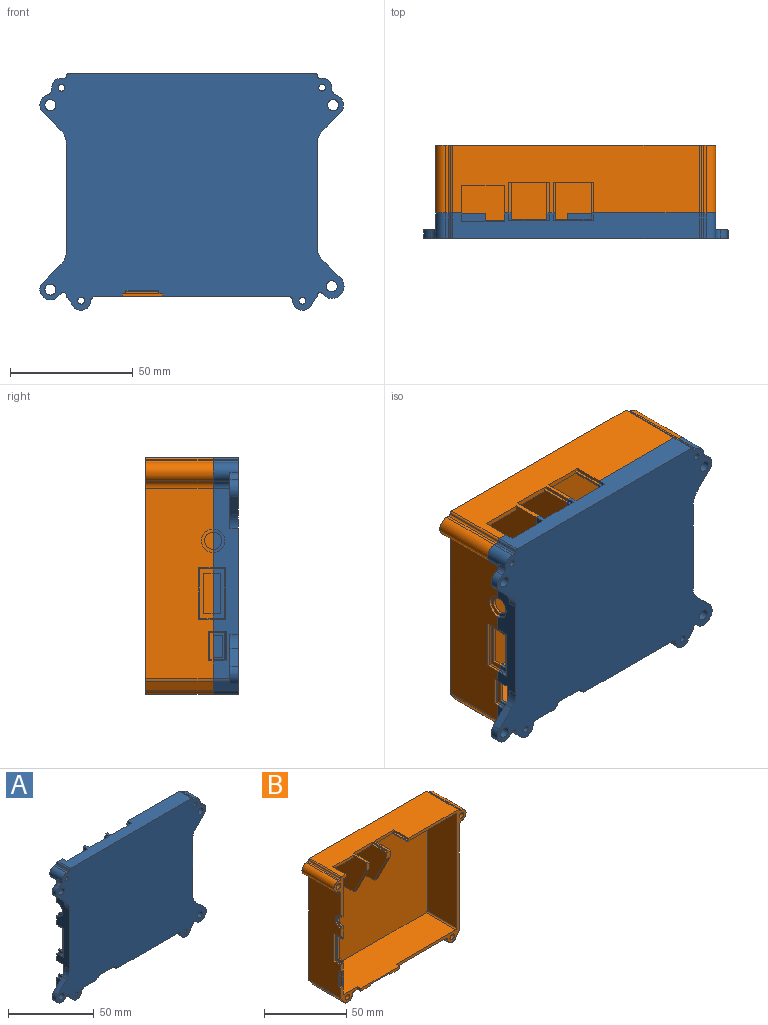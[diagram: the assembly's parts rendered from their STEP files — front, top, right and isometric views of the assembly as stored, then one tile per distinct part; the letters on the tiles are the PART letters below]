
ASSEMBLY  parts=2 mates=1
PART A: 157 faces, bbox 123.7x10.3x96.3 mm
  f0: plane 78.09x10.3mm, normal (1,0,0), area 678.6mm2, adj f1,f3,f124,f130,f138,f141,f144,f147
  f1: cylinder r=3mm len=6.8mm, axis (0,1,0), area 29.1mm2, adj f0,f2,f130,f147
  f2: cylinder r=3.9mm len=10.3mm, axis (0,1,0), area 101.4mm2, adj f1,f3,f123,f130,f136,f147
  f3: plane 123.68x96.25mm, normal (0,-1,0), area 9747mm2, adj f0,f2,f6,f9,f10,f11,f18,f19
  f4: plane 98x86.6mm, normal (0,1,0), area 8334.6mm2, adj f5,f21,f36,f37,f44,f46,f48,f49
  f5: plane 61.85x8.3mm, normal (0,0,1), area 483.4mm2, adj f4,f35,f50,f130,f132,f133
  f6: plane 50.96x10.3mm, normal (0,0,-1), area 499.3mm2, adj f3,f32,f50,f126,f130,f132
  f7: plane 22.79x10.75mm, normal (0,1,0), area 100.2mm2, adj f10,f11,f56,f86,f87,f88,f89,f90
  f8: plane 20.07x10.76mm, normal (0,1,0), area 93.7mm2, adj f9,f56,f91,f92,f93,f94,f95,f96
  f9: cylinder r=2.25mm len=4.5mm, axis (0,-1,0), area 49.5mm2, adj f3,f8
  f10: cylinder r=2.25mm len=4.5mm, axis (0,-1,0), area 49.5mm2, adj f3,f7
  f11: cylinder r=3.9mm len=10.3mm, axis (0,-1,0), area 101.4mm2, adj f3,f7,f14,f86,f90,f102
  f12: plane 3x2.8mm, normal (0,1,0), area 7.2mm2, adj f20,f23,f25,f30,f112,f113
  f13: plane 3.5x3mm, normal (0,1,0), area 8.1mm2, adj f24,f27,f29,f30,f113,f114,f117,f119
  f14: plane 30.25x10.45mm, normal (0,1,0), area 99.5mm2, adj f11,f19,f21,f30,f52,f53,f54,f55
  f15: plane 8.65x2.5mm, normal (0,1,0), area 15.1mm2, adj f52,f56,f58,f59,f60,f61,f63,f64
  f16: plane 9.75x2.5mm, normal (0,1,0), area 16.8mm2, adj f52,f53,f54,f55,f56,f61,f64,f70
  f17: plane 15.1x14.15mm, normal (0,1,0), area 78mm2, adj f18,f31,f49,f51,f52,f56,f60,f62
  f18: cylinder r=1.4mm len=10.3mm, axis (0,-1,0), area 90.6mm2, adj f3,f17
  f19: cylinder r=1.4mm len=10.3mm, axis (0,-1,0), area 90.6mm2, adj f3,f14
  f20: plane 3.6x3mm, normal (-1,0,0), area 8.7mm2, adj f12,f21,f22,f25,f30,f111
  f21: plane 97x8.3mm, normal (0,0,-1), area 654.8mm2, adj f4,f14,f20,f22,f23,f26,f27,f28
  f22: plane 2.8x2mm, normal (0,-0.45,-0.89), area 6.3mm2, adj f20,f21,f23,f25
  f23: plane 2.55x1.8mm, normal (1,0,0), area 3.5mm2, adj f12,f21,f22,f25,f113,f118
  f24: plane 3.5x0.55mm, normal (0,0,-1), area 1.9mm2, adj f13,f26,f27,f119
  f25: plane 2.8x0.55mm, normal (0,0,-1), area 1.5mm2, adj f12,f20,f22,f23
  f26: plane 3.5x2mm, normal (0,-0.45,-0.89), area 7.8mm2, adj f21,f24,f27,f119
  f27: plane 2.55x1.8mm, normal (1,0,0), area 3.5mm2, adj f13,f21,f24,f26,f28,f29
  f28: plane 14.5x0.8mm, normal (0,1,0), area 11.6mm2, adj f21,f27,f29,f131
  f29: plane 16.5x3.17mm, normal (0,0,1), area 16.5mm2, adj f13,f27,f28,f116,f117,f129,f130,f131
  f30: plane 100.4x10.3mm, normal (0,0,1), area 866.9mm2, adj f3,f12,f13,f14,f20,f100,f110,f111
  f31: plane 10.76x10.3mm, normal (0,0,-1), area 85.3mm2, adj f3,f17,f99,f104,f105,f109
  f32: plane 7.3x1mm, normal (-1,0,0), area 7.3mm2, adj f3,f6,f33,f50
  f33: plane 7.3x1.5mm, normal (0,0,-1), area 10.9mm2, adj f3,f32,f35,f50
  f34: plane 7.3x1.5mm, normal (0,0,-1), area 11mm2, adj f3,f105,f106,f109
  f35: plane 7.3x1mm, normal (-1,0,0), area 7.3mm2, adj f3,f5,f33,f36,f50
  f36: cylinder r=0.5mm len=2mm, axis (0,-1,0), area 1.6mm2, adj f3,f4,f35,f108
  f37: cone r=3.15mm half-angle=45deg, axis (0,-1,0), area 14mm2, adj f4,f38
  f38: cylinder r=2.9mm len=5.8mm, axis (0,1,0), area 63.8mm2, adj f37,f40
  f39: plane 5.8x5.8mm, normal (0,1,0), area 23.3mm2, adj f43,f151
  f40: plane 5.8x5.8mm, normal (0,1,0), area 23.3mm2, adj f38,f153
  f41: plane 5.8x5.8mm, normal (0,1,0), area 23.3mm2, adj f45,f149
  f42: plane 5.8x5.8mm, normal (0,1,0), area 23.3mm2, adj f47,f155
  f43: cylinder r=2.9mm len=5.8mm, axis (0,1,0), area 63.8mm2, adj f39,f44
  f44: cone r=3.15mm half-angle=45deg, axis (0,-1,0), area 14mm2, adj f4,f43
  f45: cylinder r=2.9mm len=5.8mm, axis (0,1,0), area 63.8mm2, adj f41,f46
  f46: cone r=3.15mm half-angle=45deg, axis (0,-1,0), area 14mm2, adj f4,f45
  f47: cylinder r=2.9mm len=5.8mm, axis (0,1,0), area 63.8mm2, adj f42,f48
  f48: cone r=3.15mm half-angle=45deg, axis (0,-1,0), area 14mm2, adj f4,f47
  f49: plane 21.65x8.3mm, normal (0,0,1), area 149.7mm2, adj f4,f17,f51,f104,f105,f106
  f50: plane 10x2mm, normal (0,1,0), area 18.5mm2, adj f5,f6,f32,f33,f35,f132
  f51: cylinder r=0.5mm len=8.3mm, axis (0,1,0), area 6.5mm2, adj f4,f17,f49,f52
  f52: plane 85.6x8.3mm, normal (1,0,0), area 494.1mm2, adj f4,f14,f15,f16,f17,f51,f53,f65
  f53: cylinder r=3.5mm len=7mm, axis (-1,0,0), area 11mm2, adj f14,f16,f52,f54
  f54: plane 9.5x4.75mm, normal (-1,0,0), area 16.2mm2, adj f14,f16,f53,f55
  f55: cylinder r=4.75mm len=9.5mm, axis (-1,0,0), area 14.9mm2, adj f14,f16,f54,f56
  f56: plane 77.46x10.3mm, normal (-1,0,0), area 472.5mm2, adj f3,f7,f8,f14,f15,f16,f17,f55
  f57: plane 10.3x0.18mm, normal (-1,0,0), area 1.9mm2, adj f3,f14,f100,f101
  f58: plane 5.12x1mm, normal (0,0,1), area 5.1mm2, adj f15,f56,f59,f84
  f59: plane 5.12x0.5mm, normal (-0.71,0,0.71), area 3.4mm2, adj f15,f58,f61,f85
  f60: plane 11x4.75mm, normal (-1,0,0), area 18.5mm2, adj f15,f17,f62,f68,f69,f76,f79,f80
  f61: plane 20x4.62mm, normal (-1,0,0), area 40.9mm2, adj f15,f16,f59,f70,f71,f72,f82,f85
  f62: plane 3.75x1mm, normal (0,0,1), area 3.8mm2, adj f17,f60,f63,f69
  f63: plane 14x5.25mm, normal (1,0,0), area 39.8mm2, adj f15,f17,f62,f65,f66,f67,f68,f69
  f64: plane 23x3.62mm, normal (1,0,0), area 31.8mm2, adj f15,f16,f70,f71,f72,f73,f74,f75
  f65: plane 5.75x0.5mm, normal (0.71,0,-0.71), area 3.9mm2, adj f17,f52,f63,f66
  f66: plane 15x0.5mm, normal (0.71,-0.71,0), area 10.3mm2, adj f52,f63,f65,f67
  f67: plane 5.75x0.5mm, normal (0.71,0,0.71), area 3.9mm2, adj f15,f52,f63,f66
  f68: plane 3.75x1mm, normal (0,0,-1), area 3.8mm2, adj f15,f60,f63,f69
  f69: plane 9x1mm, normal (0,1,0), area 9mm2, adj f60,f62,f63,f68
  f70: plane 3.12x1mm, normal (0,0,-1), area 3.1mm2, adj f16,f61,f64,f71
  f71: plane 16.5x1mm, normal (0,1,0), area 16.5mm2, adj f61,f64,f70,f72
  f72: plane 3.12x1mm, normal (0,0,1), area 3.1mm2, adj f15,f61,f64,f71
  f73: plane 4.62x0.5mm, normal (0.71,0,-0.71), area 2.9mm2, adj f15,f52,f64,f74
  f74: plane 24x1mm, normal (0.89,-0.45,0), area 26.3mm2, adj f52,f64,f73,f75
  f75: plane 4.62x0.5mm, normal (0.71,0,0.71), area 2.9mm2, adj f16,f52,f64,f74
  f76: plane 5.25x0.5mm, normal (-0.71,0,-0.71), area 3.5mm2, adj f15,f60,f77,f79
  f77: plane 5.25x1mm, normal (0,0,-1), area 5.2mm2, adj f15,f56,f76,f78
  f78: plane 12x1mm, normal (0,1,0), area 12mm2, adj f56,f77,f79,f81
  f79: plane 12x0.5mm, normal (-0.71,0.71,0), area 8.1mm2, adj f60,f76,f78,f80
  f80: plane 5.25x0.5mm, normal (-0.71,0,0.71), area 3.5mm2, adj f17,f60,f79,f81
  f81: plane 5.25x1mm, normal (0,0,1), area 5.2mm2, adj f17,f56,f78,f80
  f82: plane 5.12x0.5mm, normal (-0.71,0,-0.71), area 3.4mm2, adj f16,f61,f83,f85
  f83: plane 5.12x1mm, normal (0,0,-1), area 5.1mm2, adj f16,f56,f82,f84
  f84: plane 21x1mm, normal (0,1,0), area 21mm2, adj f56,f58,f83,f85
  f85: plane 21x0.5mm, normal (-0.71,0.71,0), area 14.5mm2, adj f59,f61,f82,f84
  f86: cylinder r=3mm len=6.8mm, axis (0,-1,0), area 29.1mm2, adj f7,f11,f14,f56
  f87: cylinder r=8mm len=5.66mm, axis (0,-1,0), area 22mm2, adj f3,f7,f56,f88
  f88: plane 7.16x7.16mm, normal (-0.71,0,-0.71), area 35.5mm2, adj f3,f7,f87,f89
  f89: cylinder r=4.25mm len=7.02mm, axis (0,-1,0), area 30mm2, adj f3,f7,f88,f90
  f90: cylinder r=3mm len=3.5mm, axis (0,-1,0), area 13.4mm2, adj f3,f7,f11,f89
  f91: cylinder r=8mm len=5.66mm, axis (0,1,0), area 22mm2, adj f3,f8,f56,f92
  f92: plane 7.16x7.16mm, normal (-0.71,0,0.71), area 35.5mm2, adj f3,f8,f91,f93
  f93: cylinder r=4.25mm len=7.26mm, axis (0,-1,0), area 46.7mm2, adj f3,f8,f92,f94
  f94: plane 3.5x1.45mm, normal (0.71,0,-0.71), area 7.2mm2, adj f3,f8,f93,f95
  f95: cylinder r=1.2mm len=3.5mm, axis (0,-1,0), area 9.6mm2, adj f3,f8,f94,f96
  f96: cylinder r=2mm len=10.3mm, axis (0,-1,0), area 12.1mm2, adj f3,f8,f17,f56,f95,f97
  f97: plane 10.3x3.48mm, normal (-0.82,0,-0.58), area 43.8mm2, adj f3,f17,f96,f98
  f98: cylinder r=3.9mm len=10.3mm, axis (0,-1,0), area 99.9mm2, adj f3,f17,f97,f99
  f99: cylinder r=2mm len=10.3mm, axis (0,-1,0), area 31.5mm2, adj f3,f17,f31,f98
  f100: cylinder r=0.8mm len=10.3mm, axis (0,1,0), area 12.9mm2, adj f3,f14,f30,f57
  f101: cylinder r=0.8mm len=10.3mm, axis (0,1,0), area 12.9mm2, adj f3,f14,f57,f102
  f102: plane 10.3x1.2mm, normal (0,0,1), area 12.4mm2, adj f3,f11,f14,f101
  f103: cylinder r=0.5mm len=8.3mm, axis (0,-1,0), area 6.5mm2, adj f4,f14,f21,f52
  f104: plane 3x2mm, normal (1,0,0), area 6mm2, adj f17,f31,f49,f105
  f105: plane 10x2mm, normal (0,1,0), area 18.5mm2, adj f31,f34,f49,f104,f106,f109
  f106: plane 7.3x1mm, normal (1,0,0), area 7.3mm2, adj f3,f34,f49,f105,f107
  f107: cylinder r=0.5mm len=2mm, axis (0,-1,0), area 1.6mm2, adj f3,f4,f106,f108
  f108: plane 12.5x2mm, normal (0,0,-1), area 25mm2, adj f3,f4,f36,f107
  f109: plane 7.3x1mm, normal (1,0,0), area 7.3mm2, adj f3,f31,f34,f105
  f110: plane 3.6x2mm, normal (1,0,0), area 7.2mm2, adj f14,f21,f30,f111
  f111: plane 17.4x2mm, normal (0,1,0), area 34.8mm2, adj f20,f21,f30,f110
  f112: plane 3.17x1.2mm, normal (1,0,0), area 3.8mm2, adj f12,f30,f113,f115
  f113: plane 16.5x3.17mm, normal (0,0,1), area 16.5mm2, adj f12,f13,f23,f112,f114,f115,f118,f119
  f114: plane 3.17x1.2mm, normal (-1,0,0), area 3.8mm2, adj f13,f30,f113,f115
  f115: plane 16.5x1.2mm, normal (0,1,0), area 19.8mm2, adj f30,f112,f113,f114
  f116: plane 16.5x1.2mm, normal (0,1,0), area 19.8mm2, adj f29,f30,f117,f129
  f117: plane 3.17x1.2mm, normal (1,0,0), area 3.8mm2, adj f13,f29,f30,f116
  f118: plane 14.5x0.8mm, normal (0,1,0), area 11.6mm2, adj f21,f23,f113,f119
  f119: plane 2.55x1.8mm, normal (-1,0,0), area 3.5mm2, adj f13,f21,f24,f26,f113,f118
  f120: cylinder r=0.8mm len=10.3mm, axis (0,1,0), area 12.9mm2, adj f3,f30,f121,f130
  f121: plane 10.3x0.18mm, normal (1,0,0), area 1.9mm2, adj f3,f120,f122,f130
  f122: cylinder r=0.8mm len=10.3mm, axis (0,1,0), area 12.9mm2, adj f3,f121,f123,f130
  f123: plane 10.3x1.2mm, normal (0,0,1), area 12.4mm2, adj f2,f3,f122,f130
  f124: plane 10.3x3.99mm, normal (0.82,0,-0.58), area 50.3mm2, adj f0,f3,f125,f130
  f125: cylinder r=3.9mm len=10.3mm, axis (0,1,0), area 99.9mm2, adj f3,f124,f126,f130
  f126: cylinder r=2mm len=10.3mm, axis (0,1,0), area 31.5mm2, adj f3,f6,f125,f130
  f127: cylinder r=1.4mm len=10.3mm, axis (0,1,0), area 90.6mm2, adj f3,f130
  f128: cylinder r=1.4mm len=10.3mm, axis (0,1,0), area 90.6mm2, adj f3,f130
  f129: plane 3.17x1.2mm, normal (-1,0,0), area 3.8mm2, adj f29,f30,f116,f130
  f130: plane 96.25x60.25mm, normal (0,1,0), area 440.9mm2, adj f0,f1,f2,f5,f6,f21,f29,f30
  f131: plane 2.47x0.8mm, normal (-1,0,0), area 2mm2, adj f21,f28,f29,f130
  f132: plane 3x2mm, normal (-1,0,0), area 6mm2, adj f5,f6,f50,f130
  f133: cylinder r=0.5mm len=8.3mm, axis (0,-1,0), area 6.5mm2, adj f4,f5,f130,f134
  f134: plane 85.6x8.3mm, normal (-1,0,0), area 710.5mm2, adj f4,f130,f133,f135
  f135: cylinder r=0.5mm len=8.3mm, axis (0,-1,0), area 6.5mm2, adj f4,f21,f130,f134
  f136: cylinder r=3mm len=3.5mm, axis (0,1,0), area 13.4mm2, adj f2,f3,f139,f147
  f137: cylinder r=2.25mm len=4.5mm, axis (0,1,0), area 49.5mm2, adj f3,f147
  f138: cylinder r=8mm len=5.66mm, axis (0,1,0), area 22mm2, adj f0,f3,f140,f147
  f139: cylinder r=4.25mm len=7.02mm, axis (0,1,0), area 30mm2, adj f3,f136,f140,f147
  f140: plane 7.16x7.16mm, normal (0.71,0,-0.71), area 35.5mm2, adj f3,f138,f139,f147
  f141: cylinder r=8mm len=5.66mm, axis (0,1,0), area 22mm2, adj f0,f3,f142,f148
  f142: plane 6.05x6.05mm, normal (0.71,0,0.71), area 29.9mm2, adj f3,f141,f145,f148
  f143: cylinder r=2.25mm len=4.5mm, axis (0,1,0), area 49.5mm2, adj f3,f148
  f144: cylinder r=1.2mm len=3.5mm, axis (0,1,0), area 9.9mm2, adj f0,f3,f146,f148
  f145: cylinder r=4.99mm len=9.34mm, axis (0,1,0), area 54.9mm2, adj f3,f142,f146,f148
  f146: plane 3.5x1.45mm, normal (-0.71,0,-0.71), area 7.2mm2, adj f3,f144,f145,f148
  f147: plane 22.79x10.75mm, normal (0,1,0), area 100.2mm2, adj f0,f1,f2,f136,f137,f138,f139,f140
  f148: plane 21.05x10.93mm, normal (0,1,0), area 107.2mm2, adj f0,f141,f142,f143,f144,f145,f146
  f149: cylinder r=1mm len=5mm, axis (0,1,0), area 31.4mm2, adj f41,f150
  f150: plane 2x2mm, normal (0,1,0), area 3.1mm2, adj f149
  f151: cylinder r=1mm len=5mm, axis (0,1,0), area 31.4mm2, adj f39,f152
  f152: plane 2x2mm, normal (0,1,0), area 3.1mm2, adj f151
  f153: cylinder r=1mm len=5mm, axis (0,1,0), area 31.4mm2, adj f40,f154
  f154: plane 2x2mm, normal (0,1,0), area 3.1mm2, adj f153
  f155: cylinder r=1mm len=5mm, axis (0,1,0), area 31.4mm2, adj f42,f156
  f156: plane 2x2mm, normal (0,1,0), area 3.1mm2, adj f155
PART B: 110 faces, bbox 113.8x30.5x96.3 mm
  f0: cylinder r=1.9mm len=26mm, axis (0,1,0), area 310.4mm2, adj f84,f107
  f1: cylinder r=1.9mm len=26mm, axis (0,1,0), area 310.4mm2, adj f84,f105
  f2: plane 14.5x13mm, normal (0,0,-1), area 188.5mm2, adj f4,f7,f103,f109
  f3: plane 56.25x25.5mm, normal (0,0,-1), area 1253.1mm2, adj f5,f24,f84,f85,f103,f108
  f4: plane 25.8x25.5mm, normal (-1,0,0), area 537.2mm2, adj f2,f6,f12,f13,f19,f103,f109
  f5: plane 25.8x25.5mm, normal (1,0,0), area 537.2mm2, adj f3,f6,f12,f13,f18,f103,f108
  f6: plane 15x3.5mm, normal (0,0,-1), area 52.5mm2, adj f4,f5,f13,f103
  f7: plane 25.8x25.5mm, normal (1,0,0), area 537.2mm2, adj f2,f11,f22,f29,f40,f103,f109
  f8: cylinder r=1mm len=25.5mm, axis (0,-1,0), area 40.1mm2, adj f25,f27,f30,f103
  f9: cylinder r=1mm len=25.5mm, axis (0,1,0), area 40.1mm2, adj f28,f30,f31,f103
  f10: plane 27x25.5mm, normal (-1,0,0), area 549.8mm2, adj f11,f15,f20,f25,f29,f40,f103
  f11: plane 15x2.8mm, normal (0,0,-1), area 42mm2, adj f7,f10,f40,f103
  f12: plane 6x3.5mm, normal (0,-1,0), area 18.6mm2, adj f4,f5,f13,f15,f16,f17,f18,f19
  f13: plane 21x10.5mm, normal (0,-0.89,-0.45), area 82.2mm2, adj f4,f5,f6,f12
  f14: plane 113.8x96.25mm, normal (0,1,0), area 9301.3mm2, adj f15,f33,f43,f44,f45,f46,f47,f48
  f15: plane 100.4x27.5mm, normal (0,0,1), area 2151.9mm2, adj f10,f12,f14,f16,f17,f20,f21,f23
  f16: plane 12.5x1.2mm, normal (-1,0,0), area 15mm2, adj f12,f15,f19,f109
  f17: plane 12.5x1.2mm, normal (1,0,0), area 15mm2, adj f12,f15,f18,f108
  f18: plane 12.5x1mm, normal (0,0,1), area 12.5mm2, adj f5,f12,f17,f108
  f19: plane 12.5x1mm, normal (0,0,1), area 12.5mm2, adj f4,f12,f16,f109
  f20: plane 17.4x2mm, normal (0,-1,0), area 34.8mm2, adj f10,f15,f21,f25
  f21: plane 11.3x2mm, normal (1,0,0), area 22.6mm2, adj f15,f20,f25,f27
  f22: plane 12.5x1mm, normal (0,0,1), area 12.5mm2, adj f7,f23,f29,f109
  f23: plane 12.5x1.2mm, normal (1,0,0), area 15mm2, adj f15,f22,f29,f109
  f24: plane 12.5x0.8mm, normal (-1,0,0), area 10mm2, adj f3,f41,f84,f108
  f25: plane 25.5x18.95mm, normal (0,0,-1), area 286.6mm2, adj f8,f10,f20,f21,f27,f103
  f26: plane 9.75x2.5mm, normal (0,-1,0), area 16.8mm2, adj f30,f44,f50,f51,f52,f53,f54,f55
  f27: plane 30.25x10.45mm, normal (0,-1,0), area 94.5mm2, adj f8,f15,f21,f25,f30,f43,f44,f45
  f28: plane 32.75x14.2mm, normal (0,-1,0), area 96.1mm2, adj f9,f30,f31,f33,f39,f44,f55,f56
  f29: plane 6x2.8mm, normal (0,-1,0), area 15.6mm2, adj f7,f10,f15,f22,f23,f40
  f30: plane 84.6x25.5mm, normal (1,0,0), area 1951.2mm2, adj f8,f9,f26,f27,f28,f52,f62,f63
  f31: plane 96x28.5mm, normal (0,0,1), area 2548.2mm2, adj f9,f28,f32,f35,f39,f84,f87,f103
  f32: plane 3x2mm, normal (1,0,0), area 6mm2, adj f31,f33,f35,f84
  f33: plane 78.21x30.5mm, normal (0,0,-1), area 2226.2mm2, adj f14,f28,f32,f34,f35,f37,f38,f39
  f34: plane 1.5x1mm, normal (1,0,0), area 1.5mm2, adj f33,f35,f36,f38
  f35: plane 33.4x2mm, normal (0,-1,0), area 50.3mm2, adj f31,f32,f33,f34,f36,f37,f39
  f36: plane 16.5x1.5mm, normal (0,0,-1), area 24.7mm2, adj f34,f35,f37,f38
  f37: plane 1.5x1mm, normal (-1,0,0), area 1.5mm2, adj f33,f35,f36,f38
  f38: plane 16.5x1mm, normal (0,-1,0), area 16.5mm2, adj f33,f34,f36,f37
  f39: plane 3x2mm, normal (-1,0,0), area 6mm2, adj f28,f31,f33,f35
  f40: plane 21x10.5mm, normal (0,-0.89,-0.45), area 65.7mm2, adj f7,f10,f11,f29
  f41: plane 12.5x1mm, normal (0,0,1), area 12.5mm2, adj f24,f42,f84,f108
  f42: plane 12.5x1.2mm, normal (-1,0,0), area 15mm2, adj f15,f41,f84,f108
  f43: cylinder r=0.8mm len=27.5mm, axis (0,1,0), area 34.6mm2, adj f14,f15,f27,f45
  f44: plane 77.46x27.5mm, normal (-1,0,0), area 1946.2mm2, adj f14,f26,f27,f28,f46,f50,f53,f57
  f45: plane 27.5x0.18mm, normal (-1,0,0), area 4.9mm2, adj f14,f27,f43,f49
  f46: cylinder r=3mm len=27.5mm, axis (0,-1,0), area 117.6mm2, adj f14,f27,f44,f47
  f47: cylinder r=3.9mm len=27.5mm, axis (0,1,0), area 321.3mm2, adj f14,f27,f46,f48
  f48: plane 27.5x1.2mm, normal (0,0,1), area 33mm2, adj f14,f27,f47,f49
  f49: cylinder r=0.8mm len=27.5mm, axis (0,1,0), area 34.6mm2, adj f14,f27,f45,f48
  f50: cylinder r=4.75mm len=9.5mm, axis (-1,0,0), area 14.9mm2, adj f26,f27,f44,f51
  f51: plane 9.5x4.75mm, normal (-1,0,0), area 16.2mm2, adj f26,f27,f50,f52
  f52: cylinder r=3.5mm len=7mm, axis (-1,0,0), area 11mm2, adj f26,f27,f30,f51
  f53: plane 5.93x1mm, normal (0,0,-1), area 5.9mm2, adj f26,f44,f54,f58
  f54: plane 5.93x0.5mm, normal (-0.71,0,-0.71), area 4mm2, adj f26,f53,f55,f59
  f55: plane 20x5.43mm, normal (-1,0,0), area 43.8mm2, adj f26,f28,f54,f56,f59,f60,f65,f66
  f56: plane 5.93x0.5mm, normal (-0.71,0,0.71), area 4mm2, adj f28,f55,f57,f59
  f57: plane 5.93x1mm, normal (0,0,1), area 5.9mm2, adj f28,f44,f56,f58
  f58: plane 21x1mm, normal (0,-1,0), area 21mm2, adj f44,f53,f57,f59
  f59: plane 21x0.5mm, normal (-0.71,-0.71,0), area 14.5mm2, adj f54,f55,f56,f58
  f60: plane 3.93x1mm, normal (0,0,-1), area 3.9mm2, adj f26,f55,f61,f66
  f61: plane 23x5.93mm, normal (1,0,0), area 71.5mm2, adj f26,f28,f60,f62,f63,f64,f65,f66
  f62: plane 6.43x0.5mm, normal (0.71,0,0.71), area 4.4mm2, adj f26,f30,f61,f63
  f63: plane 24x0.5mm, normal (0.71,0.71,0), area 16.6mm2, adj f30,f61,f62,f64
  f64: plane 6.43x0.5mm, normal (0.71,0,-0.71), area 4.4mm2, adj f28,f30,f61,f63
  f65: plane 3.93x1mm, normal (0,0,1), area 3.9mm2, adj f28,f55,f61,f66
  f66: plane 16.5x1mm, normal (0,-1,0), area 16.5mm2, adj f55,f60,f61,f65
  f67: plane 2x1mm, normal (0,0,-1), area 2mm2, adj f28,f44,f68,f72
  f68: plane 2x0.5mm, normal (-0.71,0,-0.71), area 1.2mm2, adj f28,f67,f69,f73
  f69: plane 11x1.5mm, normal (-1,0,0), area 16.5mm2, adj f28,f68,f70,f73
  f70: plane 2x0.5mm, normal (-0.71,0,0.71), area 1.2mm2, adj f28,f69,f71,f73
  f71: plane 2x1mm, normal (0,0,1), area 2mm2, adj f28,f44,f70,f72
  f72: plane 12x1mm, normal (0,-1,0), area 12mm2, adj f44,f67,f71,f73
  f73: plane 12x0.5mm, normal (-0.71,-0.71,0), area 8.1mm2, adj f68,f69,f70,f72
  f74: cylinder r=2mm len=27.5mm, axis (0,-1,0), area 33.7mm2, adj f14,f28,f44,f75
  f75: plane 27.5x3.48mm, normal (-0.82,0,-0.58), area 116.9mm2, adj f14,f28,f74,f76
  f76: cylinder r=3.9mm len=27.5mm, axis (0,1,0), area 266.6mm2, adj f14,f28,f75,f77
  f77: cylinder r=2mm len=27.5mm, axis (0,-1,0), area 84.1mm2, adj f14,f28,f33,f76
  f78: plane 2.5x0.5mm, normal (0.71,0,-0.71), area 1.6mm2, adj f28,f30,f79,f81
  f79: plane 12x2mm, normal (1,0,0), area 24mm2, adj f28,f78,f80,f81
  f80: plane 2.5x0.5mm, normal (0.71,0,0.71), area 1.6mm2, adj f28,f30,f79,f81
  f81: plane 13x0.5mm, normal (0.71,0.71,0), area 8.8mm2, adj f30,f78,f79,f80
  f82: cylinder r=1.9mm len=26.5mm, axis (0,1,0), area 316.4mm2, adj f27,f101
  f83: cylinder r=1.9mm len=26.5mm, axis (0,-1,0), area 316.4mm2, adj f28,f102
  f84: plane 96.25x60.3mm, normal (0,-1,0), area 430.9mm2, adj f0,f1,f3,f15,f24,f31,f32,f33
  f85: cylinder r=1mm len=25.5mm, axis (0,1,0), area 40.1mm2, adj f3,f84,f86,f103
  f86: plane 84.6x25.5mm, normal (-1,0,0), area 2157.3mm2, adj f84,f85,f87,f103
  f87: cylinder r=1mm len=25.5mm, axis (0,1,0), area 40.1mm2, adj f31,f84,f86,f103
  f88: cylinder r=2mm len=27.5mm, axis (0,1,0), area 84.1mm2, adj f14,f33,f84,f89
  f89: cylinder r=3.9mm len=27.5mm, axis (0,1,0), area 266.6mm2, adj f14,f84,f88,f90
  f90: plane 27.5x3.48mm, normal (0.82,0,-0.58), area 116.9mm2, adj f14,f84,f89,f91
  f91: cylinder r=2mm len=27.5mm, axis (0,1,0), area 33.7mm2, adj f14,f84,f90,f92
  f92: plane 77.46x27.5mm, normal (1,0,0), area 2130.1mm2, adj f14,f84,f91,f93
  f93: cylinder r=3mm len=27.5mm, axis (0,1,0), area 117.6mm2, adj f14,f84,f92,f94
  f94: cylinder r=3.9mm len=27.5mm, axis (0,1,0), area 321.3mm2, adj f14,f84,f93,f95
  f95: plane 27.5x1.2mm, normal (0,0,1), area 33mm2, adj f14,f84,f94,f96
  f96: cylinder r=0.8mm len=27.5mm, axis (0,1,0), area 34.6mm2, adj f14,f84,f95,f97
  f97: plane 27.5x0.18mm, normal (1,0,0), area 5mm2, adj f14,f84,f96,f98
  f98: cylinder r=0.8mm len=27.5mm, axis (0,1,0), area 34.6mm2, adj f14,f15,f84,f97
  f99: cylinder r=2.9mm len=5.8mm, axis (0,-1,0), area 18.2mm2, adj f14,f101
  f100: cylinder r=2.9mm len=5.8mm, axis (0,-1,0), area 18.2mm2, adj f14,f102
  f101: plane 5.8x5.8mm, normal (0,1,0), area 15.1mm2, adj f82,f99
  f102: plane 5.8x5.8mm, normal (0,1,0), area 15.1mm2, adj f83,f100
  f103: plane 98x86.6mm, normal (0,-1,0), area 8328.4mm2, adj f2,f3,f4,f5,f6,f7,f8,f9
  f104: cylinder r=2.9mm len=5.8mm, axis (0,1,0), area 27.3mm2, adj f14,f105
  f105: plane 5.8x5.8mm, normal (0,1,0), area 15.1mm2, adj f1,f104
  f106: cylinder r=2.9mm len=5.8mm, axis (0,1,0), area 27.3mm2, adj f14,f107
  f107: plane 5.8x5.8mm, normal (0,1,0), area 15.1mm2, adj f0,f106
  f108: plane 16.5x2mm, normal (0,-1,0), area 31.4mm2, adj f3,f5,f15,f17,f18,f24,f41,f42
  f109: plane 16.5x2mm, normal (0,-1,0), area 31.4mm2, adj f2,f4,f7,f15,f16,f19,f22,f23
PLACE A t=(37.2,-67.41,29.15)mm
PLACE B t=(37.2,-46.61,29.15)mm
MATE fastened B.f1 <-> A.f125  axis (0,-1,0) through (133.2,-57.11,-67.6)mm
